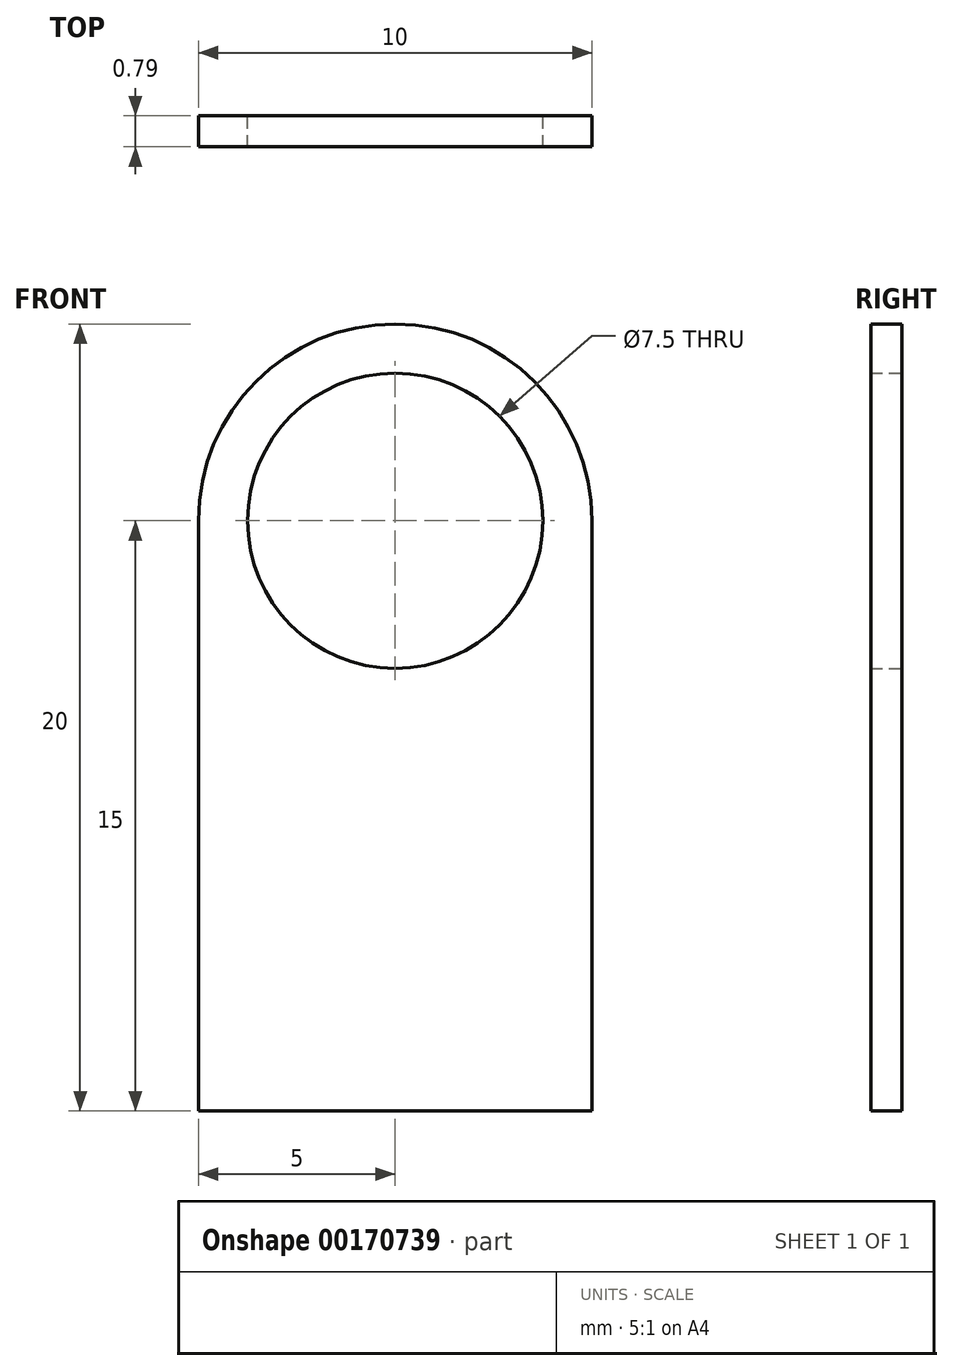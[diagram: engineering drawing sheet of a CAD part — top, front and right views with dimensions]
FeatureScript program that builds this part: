
annotation { "Feature Type Name" : "Feature", "Feature Type Description" : "" }
export const myFeature = defineFeature(function(context is Context, id is Id, definition is map)
    precondition{}
    {
        {
            var Q0;
            Q0=qCreatedBy(makeId("Front.planeOp"),FACE);
            var sketch = newSketch(context, id + "F0", { "sketchPlane" : qUnion([Q0])});
            skCircle(sketch, "E0", {"center": v(0, 0) * mm, "radius": 3.75 * mm});
            skArc(sketch, "E1", {"start": v(5, 0) * mm, "mid": v(0, 5) * mm, "end": v(-5, 0) * mm});
            skLineSegment(sketch, "E2", {"start": v(-5, 0) * mm, "end": v(-5, -15) * mm});
            skLineSegment(sketch, "E3", {"start": v(5, 0) * mm, "end": v(5, -15) * mm});
            skLineSegment(sketch, "E4", {"start": v(-5, -15) * mm, "end": v(5, -15) * mm});
            skSolve(sketch);
        }
        {
            var Q0;
            Q0 = qSketchRegion(id + "F0", true);
            extrude(context, id + "F1", {"entities" : qUnion([Q0]), "depth" : 0.79 * mm});
        }
    });
